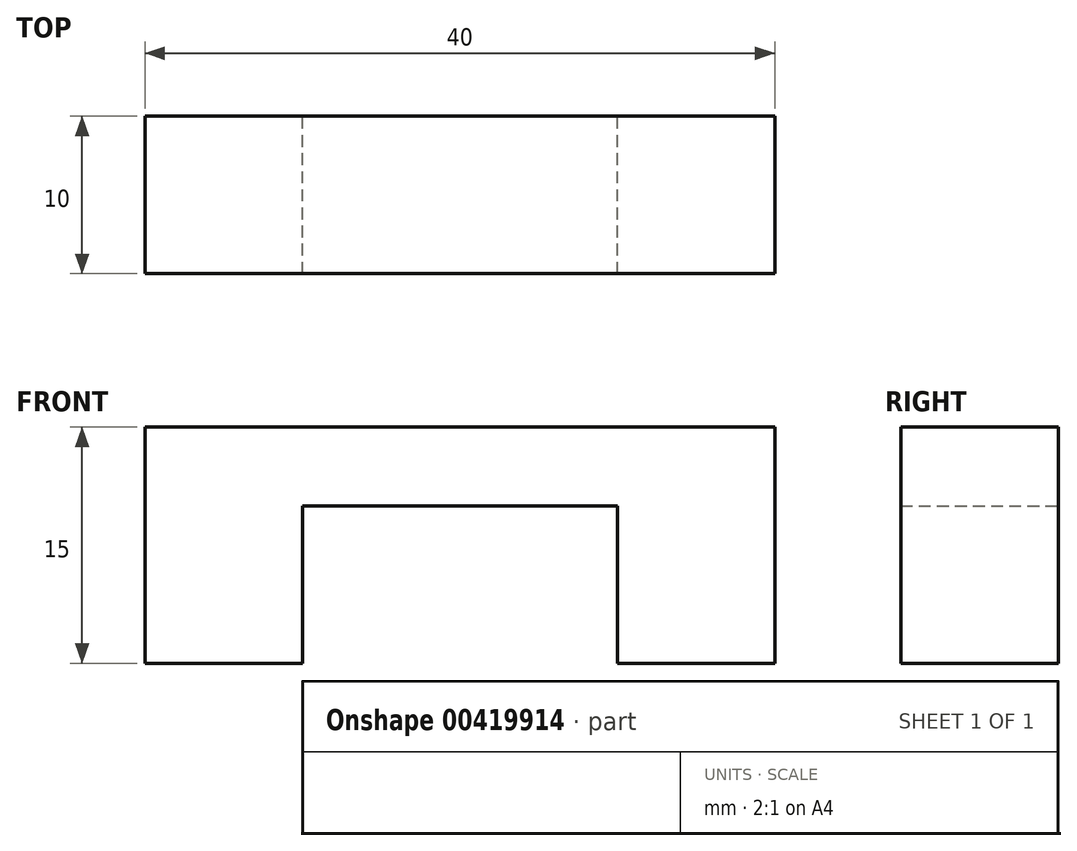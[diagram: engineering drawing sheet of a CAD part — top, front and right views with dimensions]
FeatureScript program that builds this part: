
annotation { "Feature Type Name" : "Feature", "Feature Type Description" : "" }
export const myFeature = defineFeature(function(context is Context, id is Id, definition is map)
    precondition{}
    {
        {
            var Q0;
            Q0=qCreatedBy(makeId("Top.planeOp"),FACE);
            var sketch = newSketch(context, id + "F0", { "sketchPlane" : qUnion([Q0])});
            skLineSegment(sketch, "E0.bottom", {"start": v(0, 0) * mm, "end": v(10, 0) * mm});
            skLineSegment(sketch, "E0.top", {"start": v(0, 10) * mm, "end": v(10, 10) * mm});
            skLineSegment(sketch, "E0.left", {"start": v(0, 0) * mm, "end": v(0, 10) * mm});
            skLineSegment(sketch, "E0.right", {"start": v(10, 0) * mm, "end": v(10, 10) * mm});
            skLineSegment(sketch, "E1.bottom", {"start": v(30, 0) * mm, "end": v(40, 0) * mm});
            skLineSegment(sketch, "E1.top", {"start": v(30, 10) * mm, "end": v(40, 10) * mm});
            skLineSegment(sketch, "E1.left", {"start": v(30, 0) * mm, "end": v(30, 10) * mm});
            skLineSegment(sketch, "E1.right", {"start": v(40, 0) * mm, "end": v(40, 10) * mm});
            skSolve(sketch);
        }
        {
            var Q0;
            Q0=qSketchRegion(id+"F0",true);
            extrude(context, id + "F1", {"entities" : qUnion([Q0]), "depth" : 10 * mm});
        }
        {
            var Q0;
            Q0=makeQuery(id+"F1.opExtrude","CAP_FACE",FACE,{"disambiguationData":[OSD([sQuery(id+"F0.wireOp",EDGE,"E0.bottom"),sQuery(id+"F0.wireOp",EDGE,"E0.top"),sQuery(id+"F0.wireOp",EDGE,"E0.left"),sQuery(id+"F0.wireOp",EDGE,"E0.right")])],"isStart":false});
            var sketch = newSketch(context, id + "F2", { "sketchPlane" : qUnion([Q0])});
            skLineSegment(sketch, "E2.bottom", {"start": v(0, 0) * mm, "end": v(40, 0) * mm});
            skLineSegment(sketch, "E2.top", {"start": v(0, 10) * mm, "end": v(40, 10) * mm});
            skLineSegment(sketch, "E2.left", {"start": v(0, 0) * mm, "end": v(0, 10) * mm});
            skLineSegment(sketch, "E2.right", {"start": v(40, 0) * mm, "end": v(40, 10) * mm});
            skSolve(sketch);
        }
        {
            var Q0;
            Q0=qSketchRegion(id+"F2",true);
            extrude(context, id + "F3", {"entities" : qUnion([Q0]), "operationType" : NewBodyOperationType.ADD, "depth" : 5 * mm});
        }
    });
